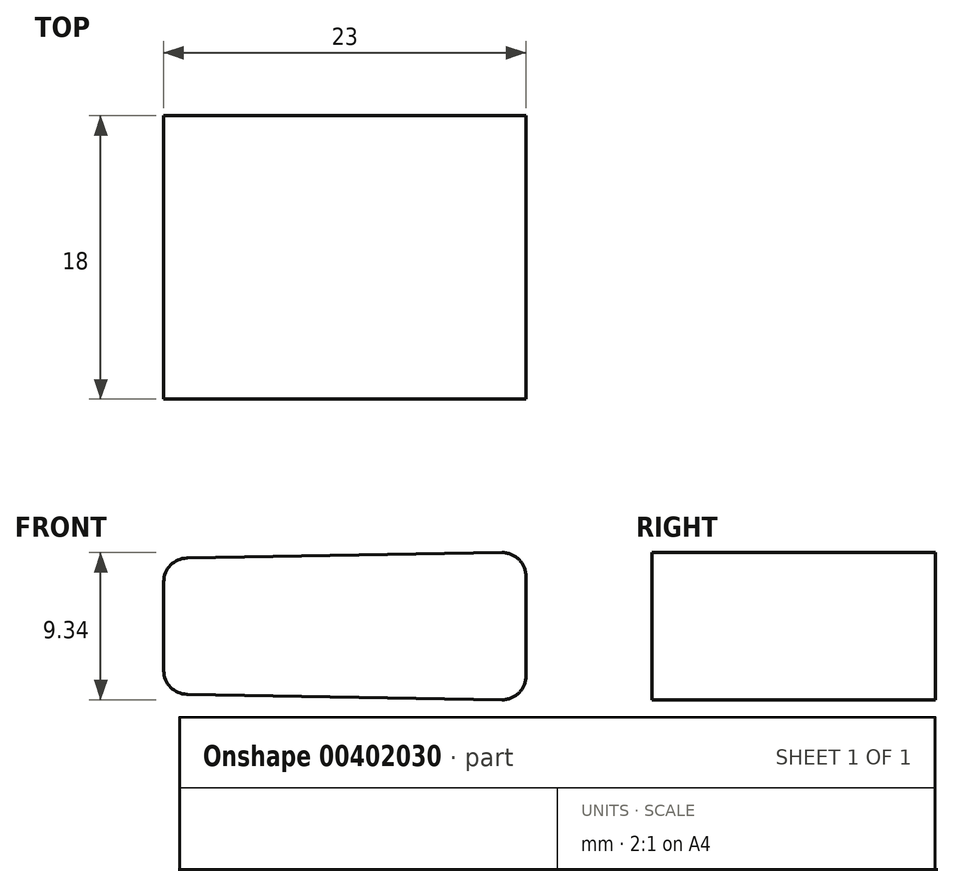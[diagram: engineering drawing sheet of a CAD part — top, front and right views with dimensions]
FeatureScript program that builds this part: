
annotation { "Feature Type Name" : "Feature", "Feature Type Description" : "" }
export const myFeature = defineFeature(function(context is Context, id is Id, definition is map)
    precondition{}
    {
        {
            var Q0;
            Q0=qCreatedBy(makeId("Front.planeOp"),FACE);
            var sketch = newSketch(context, id + "F0", { "sketchPlane" : qUnion([Q0])});
            skLineSegment(sketch, "E0", {"start": v(-11.5, -2.83) * mm, "end": v(-11.5, 2.83) * mm});
            skLineSegment(sketch, "E1", {"start": v(-10.03, 4.32) * mm, "end": v(9.97, 4.67) * mm});
            skLineSegment(sketch, "E2", {"start": v(11.5, 3.17) * mm, "end": v(11.5, -3.17) * mm});
            skLineSegment(sketch, "E3", {"start": v(9.97, -4.67) * mm, "end": v(-10.03, -4.32) * mm});
            skLineSegment(sketch, "E4", {"start": v(-37.43, 0) * mm, "end": v(29.06, 0) * mm, "construction": true});
            skLineSegment(sketch, "E5", {"start": v(0, 4.5) * mm, "end": v(0, -4.5) * mm, "construction": true});
            skPoint(sketch, "E6.visualSharp", {"position": v(-11.5, 4.3) * mm});
            skArc(sketch, "E6.filletArc", {"start": v(-10.03, 4.32) * mm, "mid": v(-11.07, 3.88) * mm, "end": v(-11.5, 2.83) * mm});
            skPoint(sketch, "E7.visualSharp", {"position": v(-11.5, -4.3) * mm});
            skArc(sketch, "E7.filletArc", {"start": v(-11.5, -2.83) * mm, "mid": v(-11.07, -3.88) * mm, "end": v(-10.03, -4.32) * mm});
            skPoint(sketch, "E8.visualSharp", {"position": v(11.5, 4.7) * mm});
            skArc(sketch, "E8.filletArc", {"start": v(11.5, 3.17) * mm, "mid": v(11.05, 4.24) * mm, "end": v(9.97, 4.67) * mm});
            skPoint(sketch, "E9.visualSharp", {"position": v(11.5, -4.7) * mm});
            skArc(sketch, "E9.filletArc", {"start": v(9.97, -4.67) * mm, "mid": v(11.05, -4.24) * mm, "end": v(11.5, -3.17) * mm});
            skSolve(sketch);
        }
        {
            var Q0;
            Q0 = qSketchRegion(id + "F0", true);
            extrude(context, id + "F1", {"entities" : qUnion([Q0]), "endBound" : BoundingType.SYMMETRIC, "depth" : 18 * mm});
        }
    });
